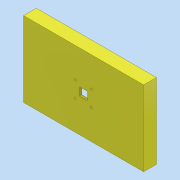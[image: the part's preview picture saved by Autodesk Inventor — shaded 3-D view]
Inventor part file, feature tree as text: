
AUTODESK INVENTOR PART (.ipt)
format: ipt  version: 2022 (Build 260153000, 153)  size: 193,536 bytes
history: native  units: mm
features: extrude x4, sketch x4
ambient origin geometry x8: Origin, YZ Plane, XZ Plane, XY Plane, X Axis, Y Axis, Z Axis, Center Point
bodies: Solid1 (feature_tree)
feature tree (8):
  extrude  "Extrusion1"  Depth=141.5mm
  extrude  "Extrusion2"  Depth=10.0mm
  extrude  "Extrusion4"  Depth=4.0mm
  extrude  "Extrusion5"  Depth=15.0mm
  sketch  "Sketch1"  dims[d0=225.5mm d1=141.5mm]
  sketch  "Sketch2"  dims[d2=10.0mm d3=10.0mm]
  sketch  "Sketch4"  dims[d5=4.0mm d6=4.0mm]
  sketch  "Sketch5"  dims[d7=24.0mm d8=0.0mm d9=5.5mm d10=7.0mm d11=0.0mm d14=4.0mm d15=0.0mm d16=15.0mm d17=15.0mm d18=3.5mm d19=2.0mm d20=0.0mm d21=15.0mm d22=15.0mm d23=7.5mm d24=7.5mm]
